# Revit family: Point d'accès Wi-Fi
name_source: partatom
category: Equipement spécialisé
units: mm (PartAtom-declared; Revit-internal decimal feet)

## family parameters
Basée sur le plan de construction = Non
Cote de connecteur circulaire = Utiliser le diamètre
Couper avec des vides une fois chargée = Non
Partagée = Oui
Point de calcul de pièce = Non
Toujours verticalement = Oui
Type d'élément = Normal

## types (1)
- Point d'accès Wi-Fi PoE
    Bande de fréquence (Mhz) = 2400
    CGU = https://export.legrand.com
    Classe ETIM = EC000816
    Couleur = Blanc
    Cryptage = WPA2
    EAN = 3414972013277
    Elévation par défaut = 0 mm  [stored 0 ft]
    Fabricant = LEGRAND
    Fonction = Legrand Wireless
    Fonction bridge = Oui
    Hauteur (mm) = 66 mm  [stored 0.216535 ft]
    Humidité = +95% max.
    IK = IK04
    IP = IP2X
    Largeur (mm) = 66 mm  [stored 0.216535 ft]
    Libellé BIM = Point d'accès Wi-Fi PoE
    Lien e-catalogue = https://www.legrand.fr
    Nombre d'utilisateurs = 16
    Portée en champ libre = 80 mm  [stored 0.262467 ft]
    Portée en intérieur = 20 mm  [stored 0.0656168 ft]
    Profondeur (mm) = 44 mm  [stored 0.144357 ft]
    Puissance = 20 dBm - 10 mW max
    RAL = 9003
    Référence Legrand = 033523
    Sécurité = 802.11i
    Température de fonctionnement = -5°C - 40°C
    Température de stockage = -20°C - 70°C

note: [stored X ft] marks values corroborated as IEEE doubles in the binary element streams (Revit-internal decimal feet)
